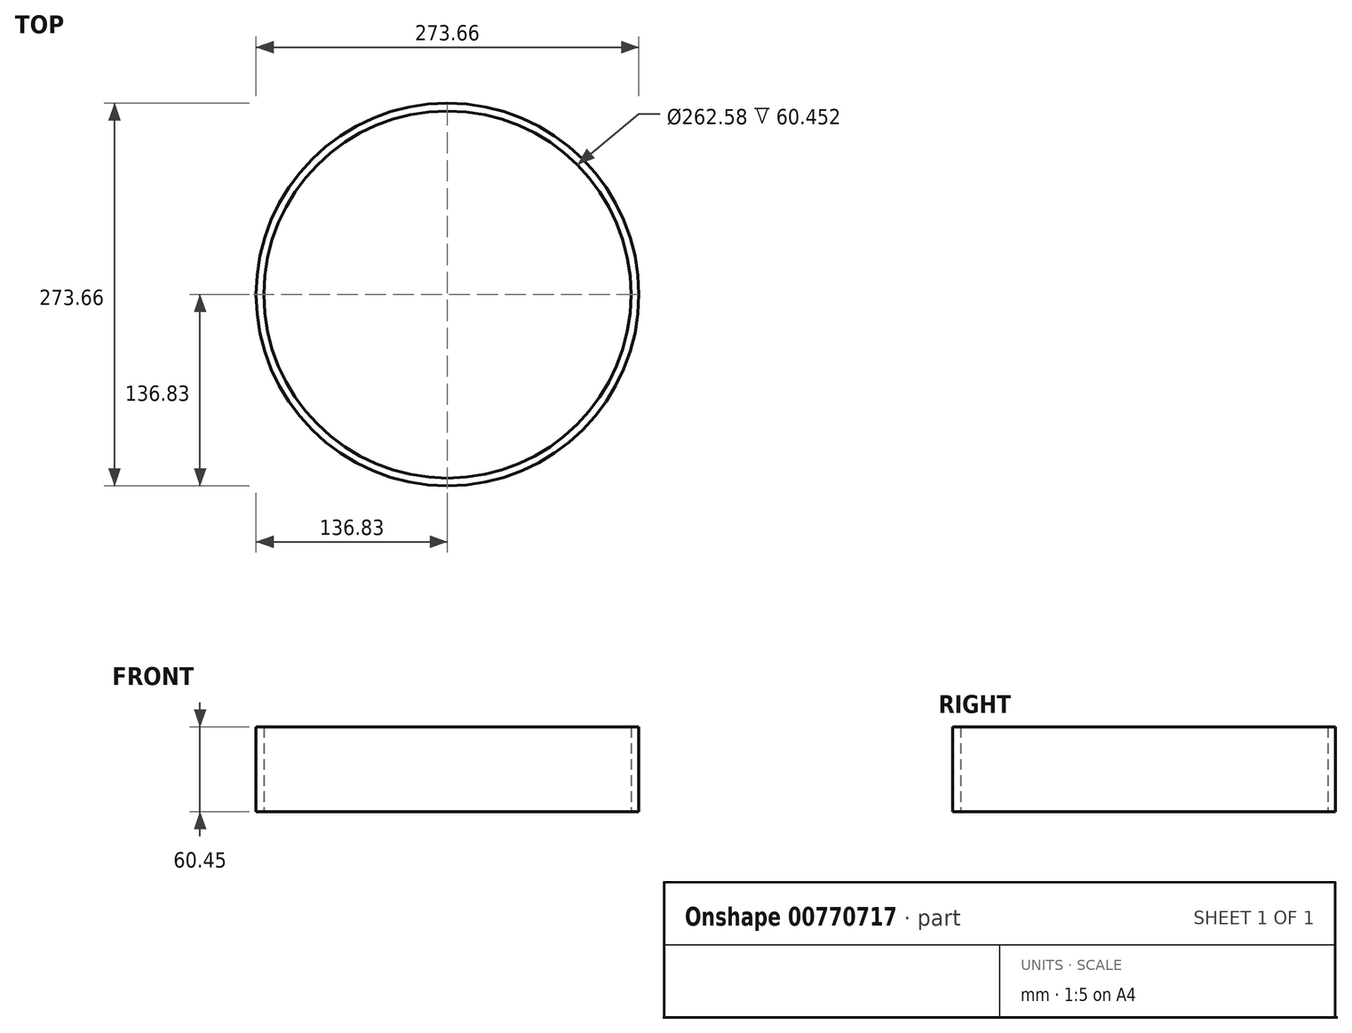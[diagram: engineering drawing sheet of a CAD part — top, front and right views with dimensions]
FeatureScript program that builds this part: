
annotation { "Feature Type Name" : "Feature", "Feature Type Description" : "" }
export const myFeature = defineFeature(function(context is Context, id is Id, definition is map)
    precondition{}
    {
        {
            var Q0;
            Q0=qCreatedBy(makeId("Top.planeOp"),FACE);
            var sketch = newSketch(context, id + "F0", { "sketchPlane" : qUnion([Q0])});
            skCircle(sketch, "E0", {"center": v(0, 0) * mm, "radius": 136.83 * mm});
            skCircle(sketch, "E1", {"center": v(0, 0) * mm, "radius": 131.3 * mm});
            skSolve(sketch);
        }
        {
            var Q0;
            Q0 = qSketchRegion(id + "F0", true);
            extrude(context, id + "F1", {"entities" : qUnion([Q0]), "depth" : 60.45 * mm, "offsetDistance" : 25.4 * mm});
        }
    });
